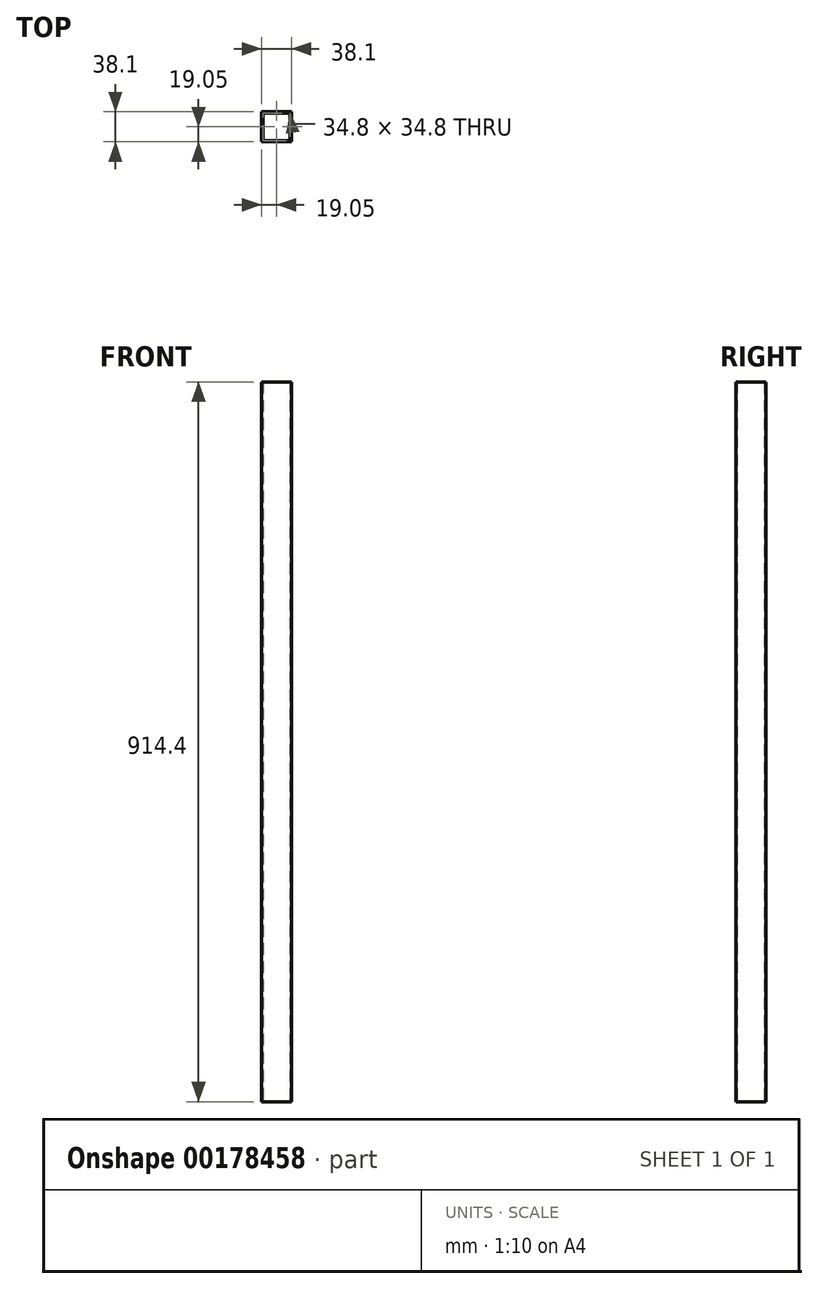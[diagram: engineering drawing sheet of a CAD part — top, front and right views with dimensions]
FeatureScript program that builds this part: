
annotation { "Feature Type Name" : "Feature", "Feature Type Description" : "" }
export const myFeature = defineFeature(function(context is Context, id is Id, definition is map)
    precondition{}
    {
        {
            var Q0;
            Q0=qCreatedBy(makeId("Top.planeOp"),FACE);
            var sketch = newSketch(context, id + "F0", { "sketchPlane" : qUnion([Q0])});
            skLineSegment(sketch, "E0.bottom", {"start": v(19.05, 19.05) * mm, "end": v(-19.05, 19.05) * mm});
            skLineSegment(sketch, "E0.top", {"start": v(19.05, -19.05) * mm, "end": v(-19.05, -19.05) * mm});
            skLineSegment(sketch, "E0.left", {"start": v(19.05, 19.05) * mm, "end": v(19.05, -19.05) * mm});
            skLineSegment(sketch, "E0.right", {"start": v(-19.05, 19.05) * mm, "end": v(-19.05, -19.05) * mm});
            skPoint(sketch, "E0.middle", {"position": v(0, 0) * mm});
            skLineSegment(sketch, "E1.bottom", {"start": v(17.4, 17.4) * mm, "end": v(-17.4, 17.4) * mm});
            skLineSegment(sketch, "E1.top", {"start": v(17.4, -17.4) * mm, "end": v(-17.4, -17.4) * mm});
            skLineSegment(sketch, "E1.left", {"start": v(17.4, 17.4) * mm, "end": v(17.4, -17.4) * mm});
            skLineSegment(sketch, "E1.right", {"start": v(-17.4, 17.4) * mm, "end": v(-17.4, -17.4) * mm});
            skSolve(sketch);
        }
        {
            var Q0;
            Q0=makeQuery(id+"F0.imprint","IMPRINT",FACE,{"disambiguationData":[TD([[makeQuery(id+"F0.imprint","IMPRINT",EDGE,{"derivedFrom":sQuery(id+"F0.wireOp",EDGE,"E0.bottom")}),1.0]])]});
            extrude(context, id + "F1", {"entities" : qUnion([Q0]), "depth" : 914.4 * mm});
        }
    });
